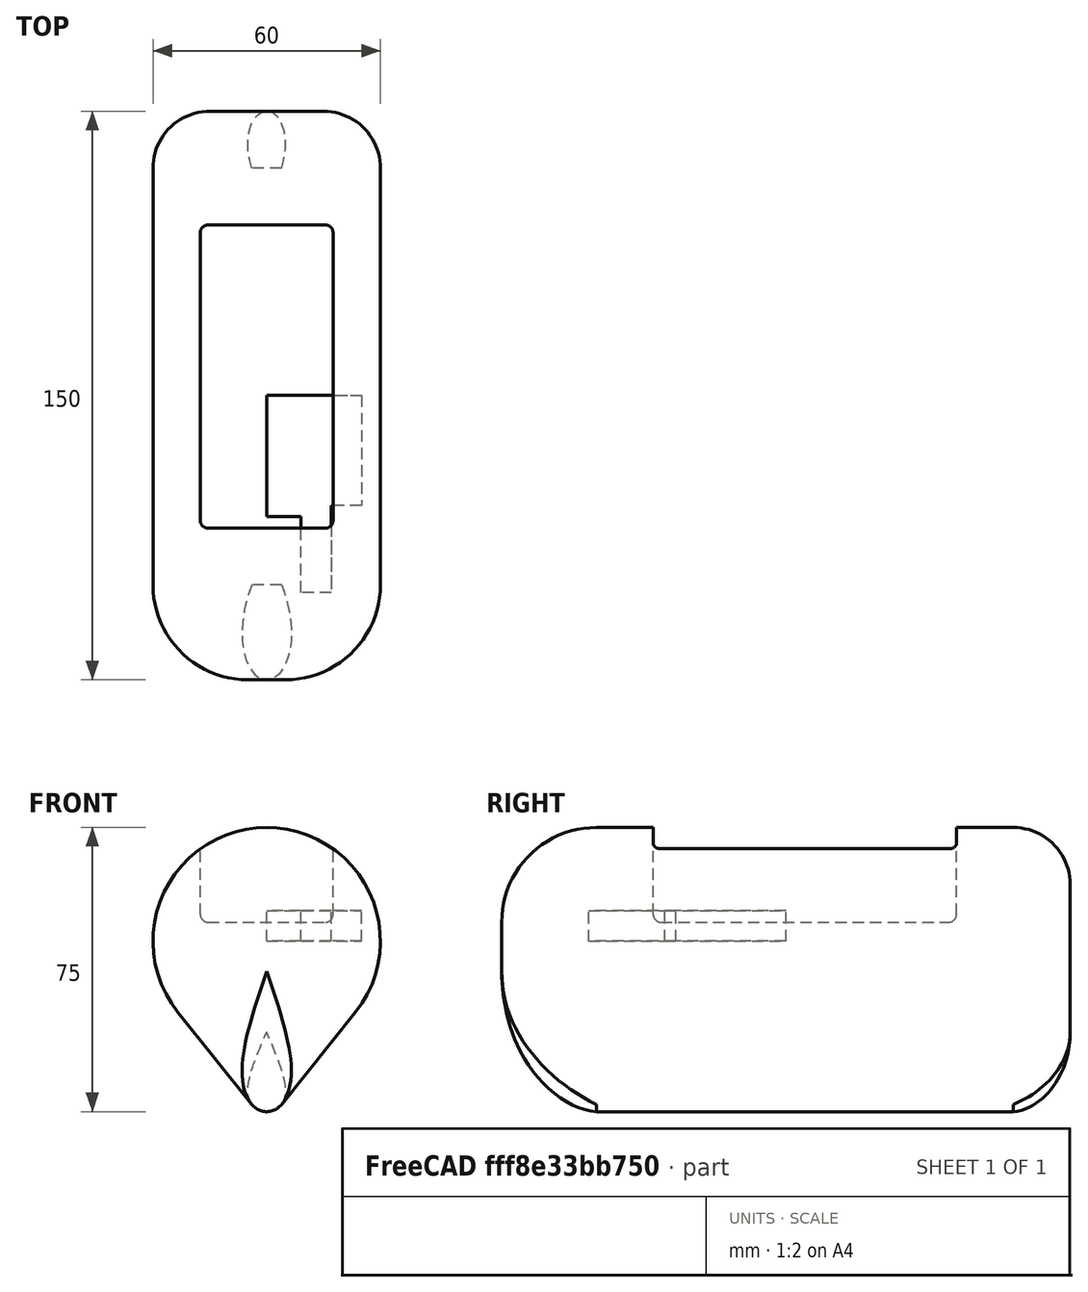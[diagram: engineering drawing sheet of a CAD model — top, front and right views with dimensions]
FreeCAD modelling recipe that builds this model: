
FCSTD DOCUMENT  (FreeCAD 0.16R6700 (Git))
Label: fuselage
License: All rights reserved
LicenseURL: http://en.wikipedia.org/wiki/All_rights_reserved
objects: Sketcher::SketchObject×3, PartDesign::Pad×3, PartDesign::Fillet×3, Part::Cut×1, Mesh::Feature×1
note: 13 computed .brp shape members not serialized (recipe doc carries the construction recipe); baked Part::Feature solids carry a one-line shape summary decoded from their .brp

FEATURE [Sketcher::SketchObject] Sketch
  Placement = pos=(-17.5,-35,5) rot=(0,0,1;0rad)
  sketch-geometry (4):
    g0: LineSegment StartX=0 StartY=80 StartZ=0 EndX=35 EndY=80 EndZ=0
    g1: LineSegment StartX=35 StartY=80 StartZ=0 EndX=35 EndY=0 EndZ=0
    g2: LineSegment StartX=35 StartY=0 StartZ=0 EndX=0 EndY=0 EndZ=0
    g3: LineSegment StartX=0 StartY=0 StartZ=0 EndX=0 EndY=80 EndZ=0
  constraints (11):
    c: Coincident(g0,g1)
    c: Coincident(g1,g2)
    c: Coincident(g2,g3)
    c: Coincident(g3,g0)
    c: Horizontal(g0)
    c: Horizontal(g2)
    c: Vertical(g1)
    c: Vertical(g3)
    c: Coincident(g2,g-1)
    c: Distance(g3) = 80
    c: Distance(g2) = 35
FEATURE [PartDesign::Pad] Pad  label="battery"
  Length = 27
  Length2 = 100
  Placement = pos=(-17.5,-35,5) rot=(0,0,1;0rad)
  Sketch = -> Sketch
  Type = 0
FEATURE [Sketcher::SketchObject] Sketch001
  sketch-geometry (10):
    g0: LineSegment StartX=0 StartY=0 StartZ=0 EndX=25 EndY=0 EndZ=0
    g1: LineSegment StartX=25 StartY=0 StartZ=0 EndX=25 EndY=-32 EndZ=0
    g2: LineSegment StartX=9 StartY=-32 StartZ=0 EndX=0 EndY=-32 EndZ=0
    g3: LineSegment StartX=0 StartY=-32 StartZ=0 EndX=0 EndY=0 EndZ=0
    g4: LineSegment StartX=25 StartY=-32 StartZ=0 EndX=25 EndY=-29 EndZ=0
    g5: LineSegment StartX=25 StartY=-29 StartZ=0 EndX=17 EndY=-29 EndZ=0
    g6: LineSegment StartX=17 StartY=-29 StartZ=0 EndX=17 EndY=-52 EndZ=0
    g7: LineSegment StartX=17 StartY=-52 StartZ=0 EndX=9 EndY=-52 EndZ=0
    g8: LineSegment StartX=9 StartY=-52 StartZ=0 EndX=9 EndY=-32 EndZ=0
    g9: LineSegment [constr] StartX=9 StartY=-32 StartZ=0 EndX=25 EndY=-32 EndZ=0
  constraints (28):
    c: Coincident(g0,g1)
    c: Coincident(g2,g3)
    c: Coincident(g3,g0)
    c: Horizontal(g0)
    c: Horizontal(g2)
    c: Vertical(g1)
    c: Vertical(g3)
    c: Distance(g0) = 25
    c: Distance(g1) = 32
    c: Coincident(g1,g4)
    c: Vertical(g4)
    c: Coincident(g4,g5)
    c: Coincident(g5,g6)
    c: Coincident(g6,g7)
    c: Coincident(g7,g8)
    c: Vertical(g8)
    c: Vertical(g6)
    c: Horizontal(g7)
    c: Horizontal(g5)
    c: DistanceX(g5,g5) = 8
    c: Distance(g7) = 8
    c: Coincident(g2,g8)
    c: Distance(g4) = 3
    c: Coincident(g9,g2)
    c: Coincident(g9,g1)
    c: Horizontal(g9)
    c: Distance(g8) = 20
    c: Coincident(g0,g-1)
FEATURE [PartDesign::Pad] Pad001  label="receiver"
  Length = 8
  Length2 = 100
  Sketch = -> Sketch001
  Type = 0
FEATURE [Sketcher::SketchObject] Sketch002
  Placement = pos=(0,0,0) rot=(1,0,0;1.5708rad)
  sketch-geometry (4):
    g0: LineSegment StartX=23.4188 StartY=-18.75 StartZ=0 EndX=3.90312 EndY=-43.125 EndZ=0
    g1: LineSegment StartX=-3.90312 StartY=-43.125 StartZ=0 EndX=-23.4188 EndY=-18.75 EndZ=0
    g2: ArcOfCircle CenterX=0 CenterY=0 CenterZ=0 NormalX=0 NormalY=0 NormalZ=1 Radius=30 StartAngle=5.60806 EndAngle=10.0999
    g3: ArcOfCircle CenterX=0 CenterY=-40 CenterZ=0 NormalX=0 NormalY=0 NormalZ=1 Radius=5 StartAngle=3.81672 EndAngle=5.60805
  constraints (14):
    c: PointOnObject(g2,g-2)
    c: Coincident(g2,g1)
    c: Coincident(g0,g2)
    c: Coincident(g1,g2)
    c: Coincident(g1,g2)
    c: Tangent(g2,g1)
    c: Tangent(g2,g0)
    c: Radius(g2) = 30
    c: Tangent(g0,g3) = 1.5708
    c: Tangent(g1,g3) = 1.5708
    c: PointOnObject(g3,g-2)
    c: Coincident(g2,g-1)
    c: Radius(g3) = 5
    c: DistanceY(g3,g-1) = 40
FEATURE [PartDesign::Pad] Pad002
  Length = 150
  Length2 = 100
  Midplane = true
  Placement = pos=(0,0,0) rot=(1,0,0;1.5708rad)
  Sketch = -> Sketch002
  Type = 0
FEATURE [PartDesign::Fillet] Fillet
  Base = -> Pad002 [Edge4,Edge7,Edge10,Edge12]
  Placement = pos=(0,0,0) rot=(1,0,0;1.5708rad)
  Radius = 25
FEATURE [PartDesign::Fillet] Fillet001  label="fuselage_shape"
  Base = -> Fillet [Edge3,Edge11,Edge12,Edge6]
  Placement = pos=(0,0,0) rot=(1,0,0;1.5708rad)
  Radius = 15
FEATURE [PartDesign::Fillet] Fillet002  label="battery_w_fillet"
  Base = -> Pad [Edge12,Edge2,Edge5,Edge6,Edge7,Edge8,Edge9,Edge10,Edge1,Edge11,Edge3,Edge4]
  Placement = pos=(-17.5,-35,5) rot=(0,0,1;0rad)
  Radius = 2
FEATURE [Part::Cut] Cut
  Base = -> Fillet001
  Tool = -> Fillet002
FEATURE [Mesh::Feature] cam_holder  label="cam+holder"
  Placement = pos=(6.5,63,7) rot=(0,0.707107,0.707107;3.14159rad)
